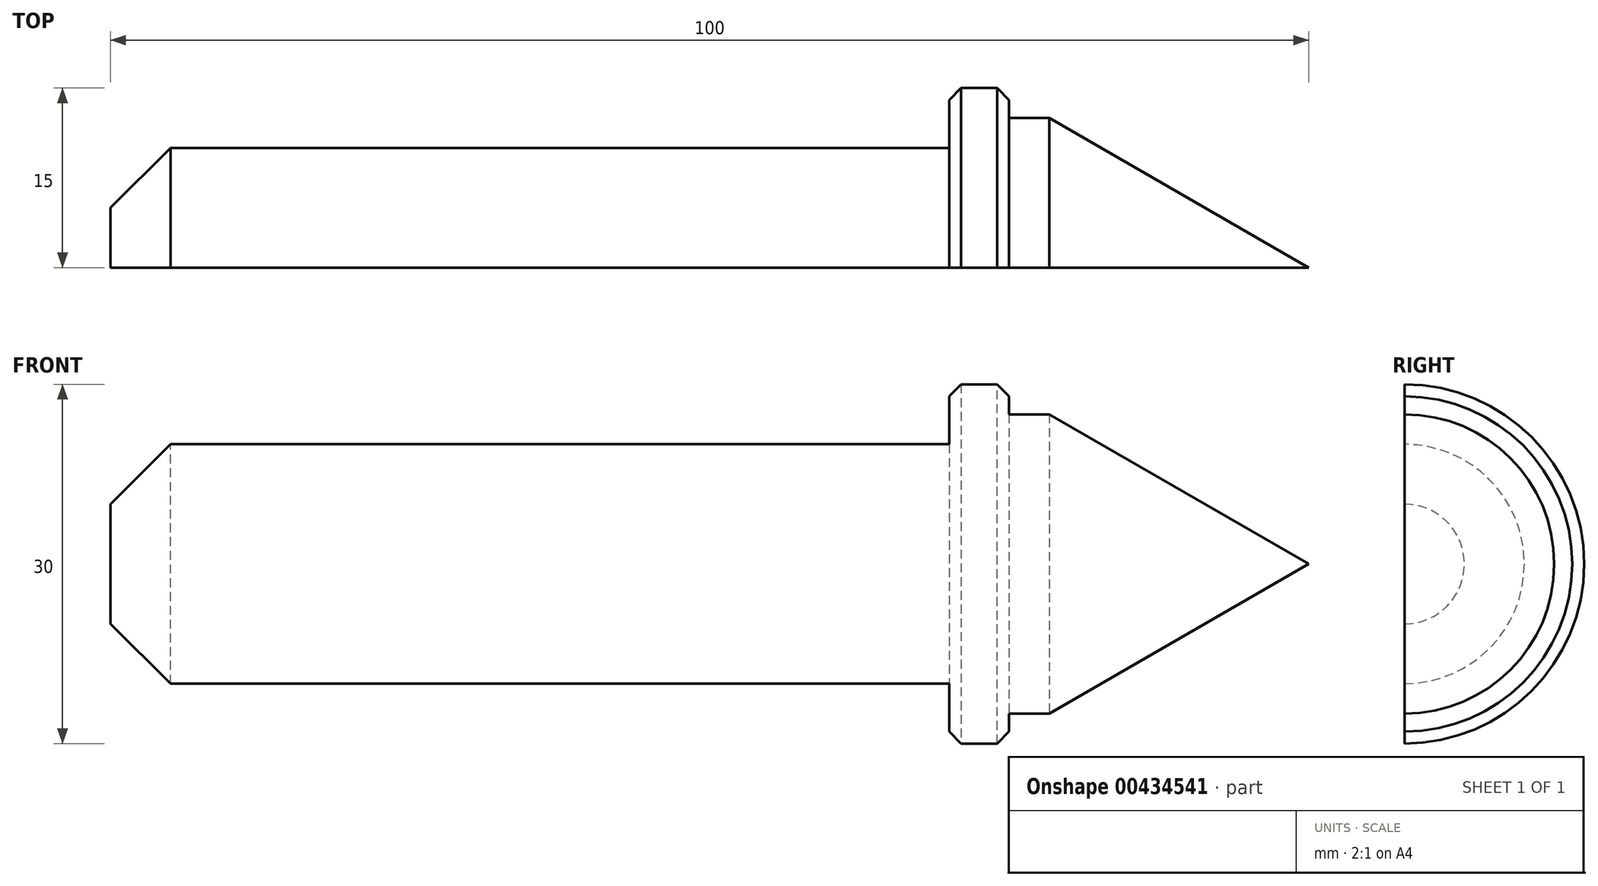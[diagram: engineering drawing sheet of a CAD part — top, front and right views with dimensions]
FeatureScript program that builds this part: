
annotation { "Feature Type Name" : "Feature", "Feature Type Description" : "" }
export const myFeature = defineFeature(function(context is Context, id is Id, definition is map)
    precondition{}
    {
        {
            var Q0;
            Q0=qCreatedBy(makeId("Front.planeOp"),FACE);
            var sketch = newSketch(context, id + "F0", { "sketchPlane" : qUnion([Q0])});
            skLineSegment(sketch, "E0", {"start": v(25, 10) * mm, "end": v(25, 0) * mm});
            skLineSegment(sketch, "E1", {"start": v(25, 0) * mm, "end": v(125, 0) * mm});
            skLineSegment(sketch, "E2", {"start": v(25, 10) * mm, "end": v(95, 10) * mm});
            skLineSegment(sketch, "E3", {"start": v(95, 10) * mm, "end": v(95, 15) * mm});
            skLineSegment(sketch, "E4", {"start": v(95, 15) * mm, "end": v(100, 15) * mm});
            skLineSegment(sketch, "E5", {"start": v(100, 15) * mm, "end": v(100, 12.5) * mm});
            skLineSegment(sketch, "E6", {"start": v(100, 12.5) * mm, "end": v(103.35, 12.5) * mm});
            skLineSegment(sketch, "E7", {"start": v(103.35, 12.5) * mm, "end": v(125, 0) * mm});
            skLineSegment(sketch, "E8", {"start": v(153.76, 12.5) * mm, "end": v(153.76, -12.5) * mm});
            skPoint(sketch, "E9", {"position": v(153.76, 0) * mm});
            skSolve(sketch);
        }
        {
            var Q0;
            Q0=makeQuery(id+"F0.imprint","IMPRINT",FACE,{"disambiguationData":[TD([[makeQuery(id+"F0.imprint","IMPRINT",EDGE,{"derivedFrom":sQuery(id+"F0.wireOp",EDGE,"E0")}),1.0]])]});
            var Q1;
            Q1=sQuery(id+"F0.wireOp",EDGE,"E1");
            revolve(context, id + "F1", {"entities" : qUnion([Q0]), "axis" : qUnion([Q1]), "revolveType" : RevolveType.FULL});
        }
        {
            var Q0;
            Q0=makeQuery(id+"F1.opRevolve","SWEPT_EDGE",EDGE,{"disambiguationData":[OSD([sQuery(id+"F0.wireOp",EDGE,"E4"),sQuery(id+"F0.wireOp",EDGE,"E5")])]});
            var Q1;
            Q1=makeQuery(id+"F1.opRevolve","SWEPT_EDGE",EDGE,{"disambiguationData":[OSD([sQuery(id+"F0.wireOp",EDGE,"E3"),sQuery(id+"F0.wireOp",EDGE,"E4")])]});
            chamfer(context, id + "F2", {"entities" : qUnion([Q0, Q1]), "width" : 1 * mm, "tangentPropagation" : true});
        }
        {
            var Q0;
            Q0=makeQuery(id+"F1.opRevolve","SWEPT_EDGE",EDGE,{"disambiguationData":[OSD([sQuery(id+"F0.wireOp",EDGE,"E0"),sQuery(id+"F0.wireOp",EDGE,"E2")])]});
            chamfer(context, id + "F3", {"entities" : qUnion([Q0]), "width" : 5 * mm, "tangentPropagation" : true});
        }
        {
            var Q0;
            Q0=qCreatedBy(makeId("Front.planeOp"),FACE);
            cPlane(context, id + "F4", {"entities" : qUnion([Q0]), "cplaneType" : CPlaneType.OFFSET, "offset" : 25 * mm, "width" : 150 * mm, "height" : 150 * mm});
        }
        {
            var Q0;
            Q0=qCreatedBy(id+"F4.planeOp",FACE);
            var sketch = newSketch(context, id + "F5", { "sketchPlane" : qUnion([Q0])});
            skLineSegment(sketch, "E10.bottom", {"start": v(-10.2, 74.46) * mm, "end": v(144.19, 74.46) * mm});
            skLineSegment(sketch, "E10.top", {"start": v(-10.2, -36.05) * mm, "end": v(144.19, -36.05) * mm});
            skLineSegment(sketch, "E10.left", {"start": v(-10.2, 74.46) * mm, "end": v(-10.2, -36.05) * mm});
            skLineSegment(sketch, "E10.right", {"start": v(144.19, 74.46) * mm, "end": v(144.19, -36.05) * mm});
            skSolve(sketch);
        }
        {
            var Q0;
            Q0 = qSketchRegion(id + "F5", true);
            extrude(context, id + "F6", {"entities" : qUnion([Q0]), "operationType" : NewBodyOperationType.REMOVE, "oppositeDirection" : true, "depth" : 25 * mm});
        }
    });
